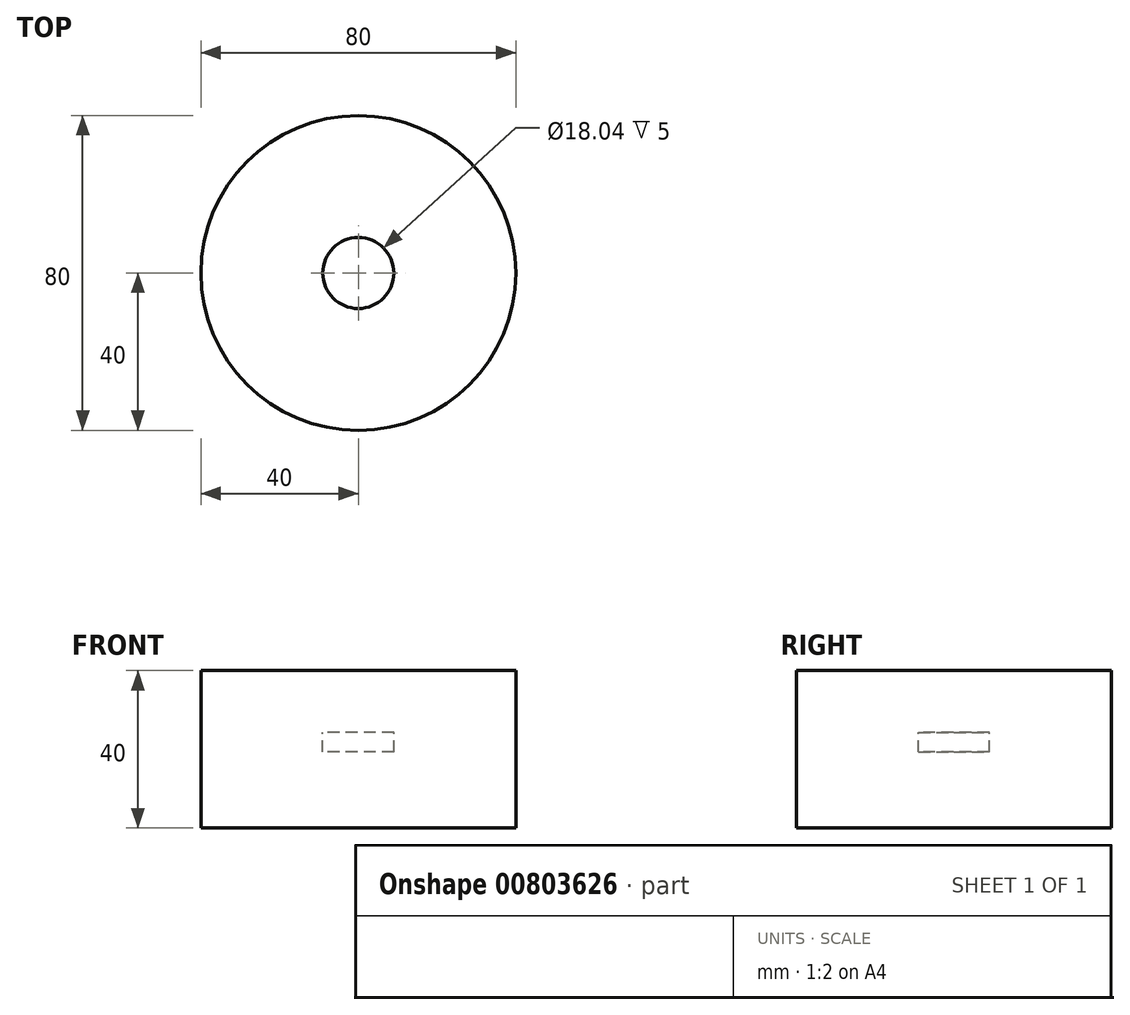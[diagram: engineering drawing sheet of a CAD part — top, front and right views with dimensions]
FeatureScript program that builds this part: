
annotation { "Feature Type Name" : "Feature", "Feature Type Description" : "" }
export const myFeature = defineFeature(function(context is Context, id is Id, definition is map)
    precondition{}
    {
        {
            var Q0;
            Q0=qCreatedBy(makeId("Front.planeOp"),FACE);
            var sketch = newSketch(context, id + "F0", { "sketchPlane" : qUnion([Q0])});
            skLineSegment(sketch, "E0", {"start": v(0, 48.85) * mm, "end": v(0, -51.15) * mm});
            skLineSegment(sketch, "E1", {"start": v(0, -51.15) * mm, "end": v(40, -51.15) * mm});
            skLineSegment(sketch, "E2", {"start": v(40, -51.15) * mm, "end": v(40, -11.15) * mm});
            skArc(sketch, "E3", {"start": v(40, -11.15) * mm, "mid": v(50, 38.85) * mm, "end": v(0, 48.85) * mm});
            skLineSegment(sketch, "E4.bottom", {"start": v(-8.98, -26.84) * mm, "end": v(9.02, -26.84) * mm});
            skLineSegment(sketch, "E4.top", {"start": v(-8.98, -31.84) * mm, "end": v(9.02, -31.84) * mm});
            skLineSegment(sketch, "E4.left", {"start": v(-8.98, -26.84) * mm, "end": v(-8.98, -31.84) * mm});
            skLineSegment(sketch, "E4.right", {"start": v(9.02, -26.84) * mm, "end": v(9.02, -31.84) * mm});
            skSolve(sketch);
        }
        {
            var Q0;
            Q0=makeQuery(id+"F0.imprint","IMPRINT",FACE,{"disambiguationData":[TD([[makeQuery(id+"F0.imprint","IMPRINT",EDGE,{"derivedFrom":sQuery(id+"F0.wireOp",EDGE,"E0")}),1.0]])]});
            var Q1;
            Q1=sQuery(id+"F0.wireOp",EDGE,"E0");
            revolve(context, id + "F1", {"surfaceOperationType" : NewSurfaceOperationType.NEW, "entities" : qUnion([Q0]), "axis" : qUnion([Q1]), "revolveType" : RevolveType.FULL});
        }
    });
